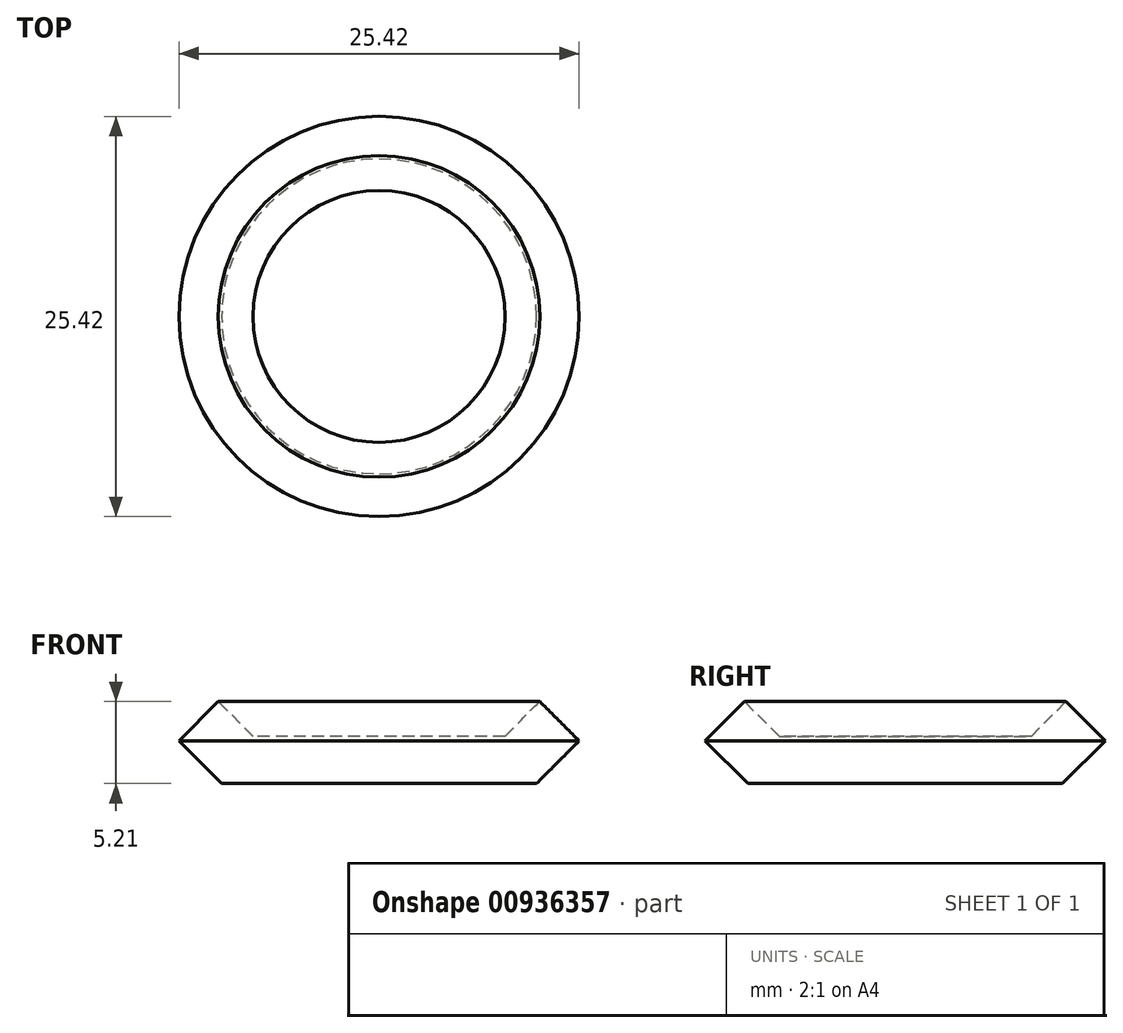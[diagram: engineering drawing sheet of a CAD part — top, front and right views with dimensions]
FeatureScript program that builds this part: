
annotation { "Feature Type Name" : "Feature", "Feature Type Description" : "" }
export const myFeature = defineFeature(function(context is Context, id is Id, definition is map)
    precondition{}
    {
        {
            var Q0;
            Q0=qCreatedBy(makeId("Front.planeOp"),FACE);
            var sketch = newSketch(context, id + "F0", { "sketchPlane" : qUnion([Q0])});
            skLineSegment(sketch, "E0", {"start": v(0, 3) * mm, "end": v(-8, 3) * mm});
            skLineSegment(sketch, "E1", {"start": v(-8, 3) * mm, "end": v(-10.21, 5.21) * mm});
            skLineSegment(sketch, "E2", {"start": v(-10.21, 5.21) * mm, "end": v(-12.71, 2.71) * mm});
            skLineSegment(sketch, "E3", {"start": v(-12.71, 2.71) * mm, "end": v(-10, 0) * mm});
            skLineSegment(sketch, "E4", {"start": v(-10, 0) * mm, "end": v(0, 0) * mm});
            skLineSegment(sketch, "E5", {"start": v(0, 3) * mm, "end": v(0, 0) * mm});
            skSolve(sketch);
        }
        {
            var Q0;
            Q0 = qSketchRegion(id + "F0", true);
            var Q1;
            Q1=sQuery(id+"F0.wireOp",EDGE,"E5");
            revolve(context, id + "F1", {"surfaceOperationType" : NewSurfaceOperationType.NEW, "entities" : qUnion([Q0]), "axis" : qUnion([Q1]), "revolveType" : RevolveType.FULL});
        }
    });
